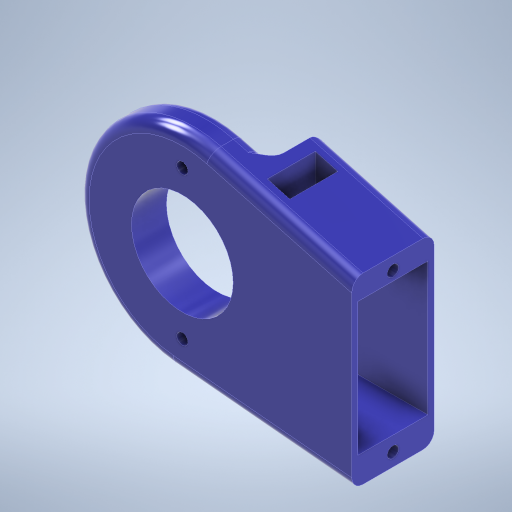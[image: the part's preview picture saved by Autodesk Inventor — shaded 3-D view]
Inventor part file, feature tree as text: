
AUTODESK INVENTOR PART (.ipt)
format: ipt  version: 2023.2 (Build 272271000, 271)  size: 370,688 bytes
history: native  units: mm
features: sketch x6, extrude x4, hole x2, fillet x1
ambient origin geometry x8: Origin, YZ Plane, XZ Plane, XY Plane, X Axis, Y Axis, Z Axis, Center Point
bodies: Solid1 (feature_tree)
feature tree (13):
  extrude  "Extrusion1"  Depth=32.4mm
  extrude  "Extrusion3"  Depth=12.4mm
  extrude  "Extrusion4"  Depth=8.5mm
  extrude  "Extrusion5"  TaperAngle=0.0deg  [1 undecoded]
  hole  "Hole2"  [1 undecoded]
  fillet  "Fillet1"  Radius=10.0mm
  hole  "Hole3"  [1 undecoded]
  sketch  "Sketch1"  dims[d2=14.6mm d3=0.0mm d13=32.4mm]
  sketch  "Sketch4"  dims[d22=8.4mm d23=0.0mm d25=12.4mm]
  sketch  "Sketch5"  dims[d26=18.0mm d27=0.0mm d28=8.5mm]
  sketch  "Sketch6"  dims[d29=4.0mm d30=0.0mm d31=0.0mm]
  sketch  "Sketch7"  dims[d32=27.8mm]
  sketch  "Sketch8"  dims[d33=2.0mm d34=6.0mm d35=4.0mm d36=2.0mm d37=90.0deg d38=7.0mm d39=0.0mm d40=37.0mm d41=10.0mm d42=30.0mm d43=2.0mm d45=5.2mm d46=18.0mm d47=26.2mm d48=2.0mm d49=6.0mm d50=4.0mm d51=2.0mm d52=90.0deg d53=8.0mm d54=0.0mm d55=27.8mm d56=22.6mm d57=23.6mm]
note: 3 required parameter values undecoded (feature->parameter linkage not recoverable at this tier; creation-order binding heuristic only, values carry confidence <= 0.55)
